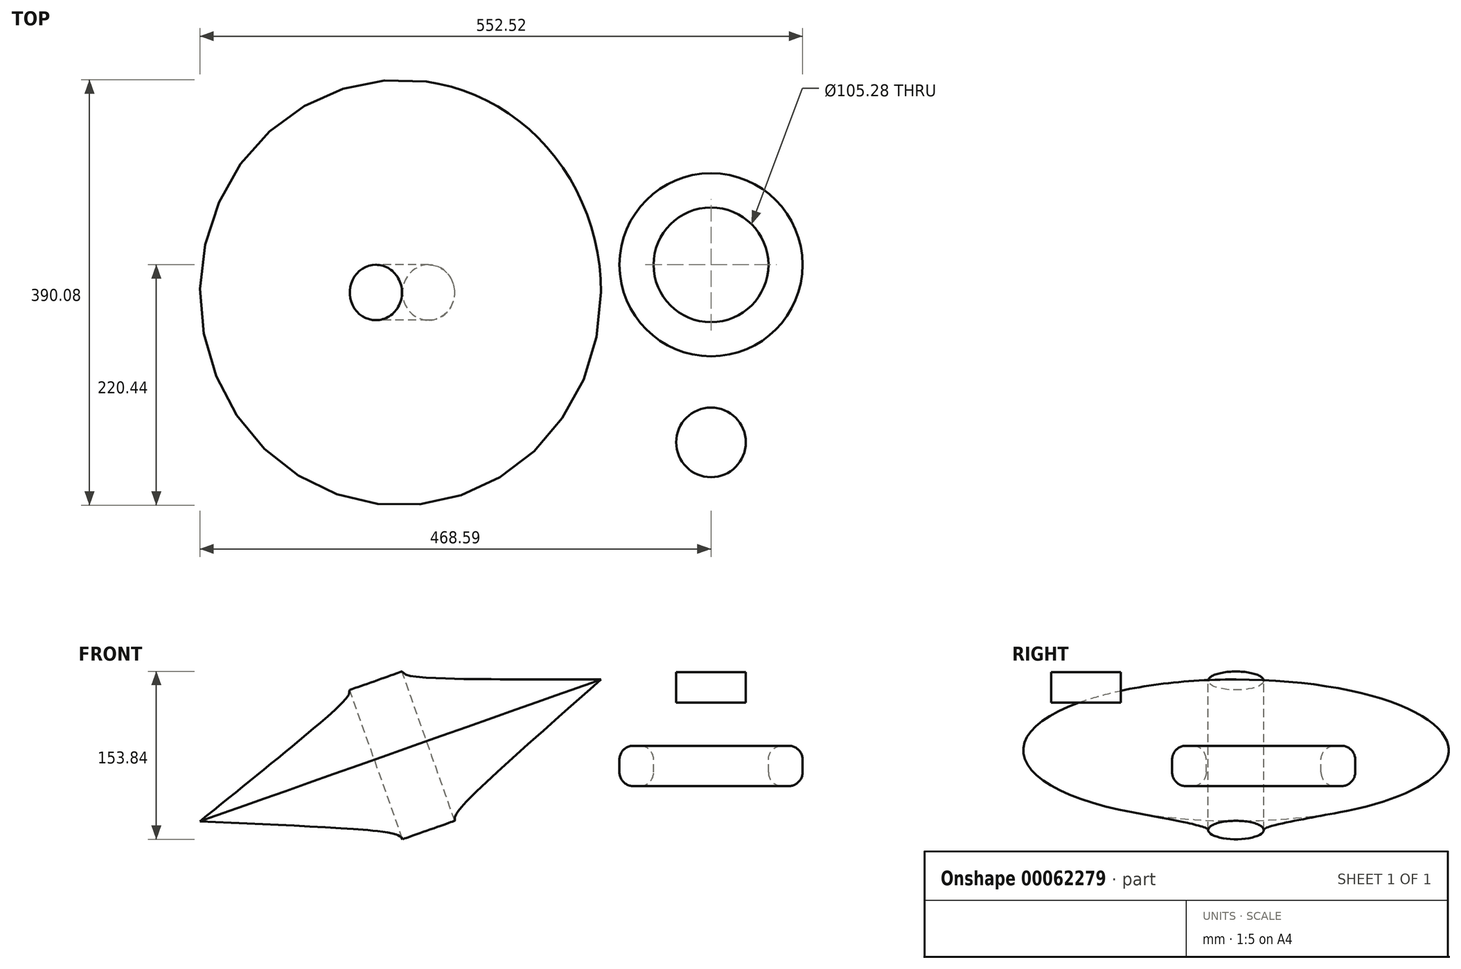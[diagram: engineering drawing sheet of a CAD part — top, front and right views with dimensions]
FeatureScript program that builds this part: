
annotation { "Feature Type Name" : "Feature", "Feature Type Description" : "" }
export const myFeature = defineFeature(function(context is Context, id is Id, definition is map)
    precondition{}
    {
        {
            var Q0;
            Q0=qCreatedBy(makeId("Front.planeOp"),FACE);
            var sketch = newSketch(context, id + "F0", { "sketchPlane" : qUnion([Q0])});
            skLineSegment(sketch, "E0.bottom", {"start": v(-47.12, 30.26) * mm, "end": v(0, 30.26) * mm});
            skLineSegment(sketch, "E0.top", {"start": v(-47.12, 0) * mm, "end": v(0, 0) * mm});
            skLineSegment(sketch, "E0.left", {"start": v(-47.12, 30.26) * mm, "end": v(-47.12, 0) * mm});
            skLineSegment(sketch, "E0.right", {"start": v(0, 30.26) * mm, "end": v(0, 0) * mm});
            skSolve(sketch);
        }
        {
            var Q0;
            Q0=sQuery(id+"F0.wireOp",EDGE,"E0.left");
            var Q1;
            Q1=sQuery(id+"F0.wireOp",EDGE,"E0.top");
            var Q2;
            Q2=sQuery(id+"F0.wireOp",EDGE,"E0.right");
            var Q3;
            Q3=sQuery(id+"F0.wireOp",EDGE,"E0.bottom");
            revolve(context, id + "F1", {"bodyType" : ToolBodyType.SURFACE, "operationType" : NewBodyOperationType.ADD, "surfaceEntities" : qUnion([Q0, Q1, Q2]), "axis" : qUnion([Q3]), "revolveType" : RevolveType.FULL});
        }
        {
            var Q0;
            Q0=qCreatedBy(makeId("Right.planeOp"),FACE);
            var sketch = newSketch(context, id + "F2", { "sketchPlane" : qUnion([Q0])});
            skLineSegment(sketch, "E1", {"start": v(0, -10.15) * mm, "end": v(0, -70.82) * mm});
            skLineSegment(sketch, "E2.bottom", {"start": v(-83.93, -20.69) * mm, "end": v(-52.64, -20.69) * mm});
            skLineSegment(sketch, "E2.top", {"start": v(-83.93, -57.72) * mm, "end": v(-52.64, -57.72) * mm});
            skLineSegment(sketch, "E2.left", {"start": v(-83.93, -20.69) * mm, "end": v(-83.93, -57.72) * mm});
            skLineSegment(sketch, "E2.right", {"start": v(-52.64, -20.69) * mm, "end": v(-52.64, -57.72) * mm});
            skSolve(sketch);
        }
        {
            var Q0;
            Q0=makeQuery(id+"F2.imprint","IMPRINT",FACE,{"disambiguationData":[TD([[makeQuery(id+"F2.imprint","IMPRINT",EDGE,{"derivedFrom":sQuery(id+"F2.wireOp",EDGE,"E2.bottom")}),-1.0]])]});
            var Q1;
            Q1=sQuery(id+"F2.wireOp",EDGE,"E1");
            revolve(context, id + "F3", {"entities" : qUnion([Q0]), "axis" : qUnion([Q1]), "revolveType" : RevolveType.FULL});
        }
        {
            var Q0;
            Q0=qCreatedBy(makeId("Right.planeOp"),FACE);
            var sketch = newSketch(context, id + "F4", { "sketchPlane" : qUnion([Q0])});
            skLineSegment(sketch, "E3.bottom", {"start": v(-194.72, 46.68) * mm, "end": v(-162.8, 46.68) * mm});
            skLineSegment(sketch, "E3.top", {"start": v(-194.72, 18.9) * mm, "end": v(-162.8, 18.9) * mm});
            skLineSegment(sketch, "E3.left", {"start": v(-194.72, 46.68) * mm, "end": v(-194.72, 18.9) * mm});
            skLineSegment(sketch, "E3.right", {"start": v(-162.8, 46.68) * mm, "end": v(-162.8, 18.9) * mm});
            skSolve(sketch);
        }
        {
            var Q0;
            Q0 = qSketchRegion(id + "F4", true);
            var Q1;
            Q1=sQuery(id+"F4.wireOp",EDGE,"E3.right");
            revolve(context, id + "F5", {"entities" : qUnion([Q0]), "axis" : qUnion([Q1]), "revolveType" : RevolveType.FULL});
        }
        {
            var Q0;
            Q0=makeQuery(id+"F3.opRevolve","SWEPT_EDGE",EDGE,{"disambiguationData":[OSD([sQuery(id+"F2.wireOp",EDGE,"E2.bottom"),sQuery(id+"F2.wireOp",EDGE,"E2.left")])]});
            fillet(context, id + "F6", {"entities" : qUnion([Q0]), "radius" : 12.7 * mm, "tangentPropagation" : true, "allowEdgeOverflow" : false});
        }
        {
            var Q0;
            Q0=makeQuery(id+"F3.opRevolve","SWEPT_EDGE",EDGE,{"disambiguationData":[OSD([sQuery(id+"F2.wireOp",EDGE,"E2.top"),sQuery(id+"F2.wireOp",EDGE,"E2.left")])]});
            fillet(context, id + "F7", {"entities" : qUnion([Q0]), "radius" : 12.7 * mm, "tangentPropagation" : true, "allowEdgeOverflow" : false});
        }
        {
            var Q0;
            Q0=makeQuery(id+"F3.opRevolve","SWEPT_EDGE",EDGE,{"disambiguationData":[OSD([sQuery(id+"F2.wireOp",EDGE,"E2.top"),sQuery(id+"F2.wireOp",EDGE,"E2.right")])]});
            var Q1;
            Q1=makeQuery(id+"F3.opRevolve","SWEPT_EDGE",EDGE,{"disambiguationData":[OSD([sQuery(id+"F2.wireOp",EDGE,"E2.bottom"),sQuery(id+"F2.wireOp",EDGE,"E2.right")])]});
            fillet(context, id + "F8", {"entities" : qUnion([Q0, Q1]), "radius" : 12.7 * mm, "tangentPropagation" : true, "allowEdgeOverflow" : false});
        }
        {
            var Q0;
            Q0=qCreatedBy(makeId("Front.planeOp"),FACE);
            var sketch = newSketch(context, id + "F9", { "sketchPlane" : qUnion([Q0])});
            skLineSegment(sketch, "E4", {"start": v(-467.02, -89.42) * mm, "end": v(-307.29, 38.93) * mm});
            skLineSegment(sketch, "E5", {"start": v(-307.29, 38.93) * mm, "end": v(-258.88, -97.98) * mm});
            skLineSegment(sketch, "E6", {"start": v(-467.02, -89.42) * mm, "end": v(-258.88, -97.98) * mm});
            skLineSegment(sketch, "E7", {"start": v(-239.35, 63.01) * mm, "end": v(-226.51, -122.13) * mm});
            skSolve(sketch);
        }
        {
            var Q0;
            Q0=makeQuery(id+"F9.imprint","IMPRINT",FACE,{"disambiguationData":[TD([[makeQuery(id+"F9.imprint","IMPRINT",EDGE,{"derivedFrom":sQuery(id+"F9.wireOp",EDGE,"E4")}),-1.0]])]});
            var Q1;
            Q1=sQuery(id+"F9.wireOp",EDGE,"E4");
            var Q2;
            Q2=sQuery(id+"F9.wireOp",EDGE,"E5");
            var Q3;
            Q3=sQuery(id+"F9.wireOp",EDGE,"E6");
            extrude(context, id + "F10", {"entities" : qUnion([Q0]), "bodyType" : ToolBodyType.SURFACE, "surfaceEntities" : qUnion([Q1, Q2, Q3]), "depth" : 25.4 * mm});
        }
        {
            var Q0;
            Q0 = qSketchRegion(id + "F9", true);
            var Q1;
            Q1=makeQuery(id+"F10.opExtrude","CAP_EDGE",EDGE,{"disambiguationData":[OSD([sQuery(id+"F9.wireOp",EDGE,"E5")])],"isStart":false});
            revolve(context, id + "F11", {"entities" : qUnion([Q0]), "axis" : qUnion([Q1]), "revolveType" : RevolveType.FULL});
        }
        {
            var Q0;
            Q0=qCreatedBy(makeId("Front.planeOp"),FACE);
            var sketch = newSketch(context, id + "F12", { "sketchPlane" : qUnion([Q0])});
            skLineSegment(sketch, "E8.bottom", {"start": v(151.7, -54.92) * mm, "end": v(232.94, -54.92) * mm});
            skLineSegment(sketch, "E8.top", {"start": v(151.7, -117.85) * mm, "end": v(232.94, -117.85) * mm});
            skLineSegment(sketch, "E8.left", {"start": v(151.7, -54.92) * mm, "end": v(151.7, -117.85) * mm});
            skLineSegment(sketch, "E8.right", {"start": v(232.94, -54.92) * mm, "end": v(232.94, -117.85) * mm});
            skLineSegment(sketch, "E9", {"start": v(151.7, -117.85) * mm, "end": v(192.32, -159.62) * mm});
            skLineSegment(sketch, "E10", {"start": v(232.94, -117.85) * mm, "end": v(192.32, -159.62) * mm});
            skSolve(sketch);
        }
        {
            var Q0;
            Q0 = qSketchRegion(id + "F12", true);
            var Q1;
            Q1=sQuery(id+"F12.wireOp",EDGE,"E8.left");
            var Q2;
            Q2=sQuery(id+"F12.wireOp",EDGE,"E8.bottom");
            var Q3;
            Q3=sQuery(id+"F12.wireOp",EDGE,"E8.right");
            var Q4;
            Q4=sQuery(id+"F12.wireOp",EDGE,"E10");
            var Q5;
            Q5=sQuery(id+"F12.wireOp",EDGE,"E9");
            extrude(context, id + "F13", {"entities" : qUnion([Q0]), "bodyType" : ToolBodyType.SURFACE, "operationType" : NewBodyOperationType.ADD, "surfaceEntities" : qUnion([Q1, Q2, Q3, Q4, Q5]), "depth" : 25.4 * mm});
        }
        {
            var Q0;
            Q0=makeQuery(id+"F13.opExtrude","CAP_EDGE",EDGE,{"disambiguationData":[OSD([sQuery(id+"F12.wireOp",EDGE,"E8.bottom")])],"isStart":false});
            var Q1;
            Q1=makeQuery(id+"F13.opExtrude","CAP_EDGE",EDGE,{"disambiguationData":[OSD([sQuery(id+"F12.wireOp",EDGE,"E8.right")])],"isStart":false});
            var Q2;
            Q2=makeQuery(id+"F13.opExtrude","CAP_EDGE",EDGE,{"disambiguationData":[OSD([sQuery(id+"F12.wireOp",EDGE,"E8.left")])],"isStart":false});
            var Q3;
            Q3=makeQuery(id+"F13.opExtrude","CAP_EDGE",EDGE,{"disambiguationData":[OSD([sQuery(id+"F12.wireOp",EDGE,"E9")])],"isStart":false});
            var Q4;
            Q4=makeQuery(id+"F13.opExtrude","CAP_EDGE",EDGE,{"disambiguationData":[OSD([sQuery(id+"F12.wireOp",EDGE,"E10")])],"isStart":false});
            var Q5;
            Q5=makeQuery(id+"F13.opExtrude","CAP_EDGE",EDGE,{"disambiguationData":[OSD([sQuery(id+"F12.wireOp",EDGE,"E8.bottom")])],"isStart":true});
            revolve(context, id + "F14", {"bodyType" : ToolBodyType.SURFACE, "operationType" : NewBodyOperationType.ADD, "surfaceEntities" : qUnion([Q0, Q1, Q2, Q3, Q4]), "axis" : qUnion([Q5]), "revolveType" : RevolveType.FULL});
        }
    });
